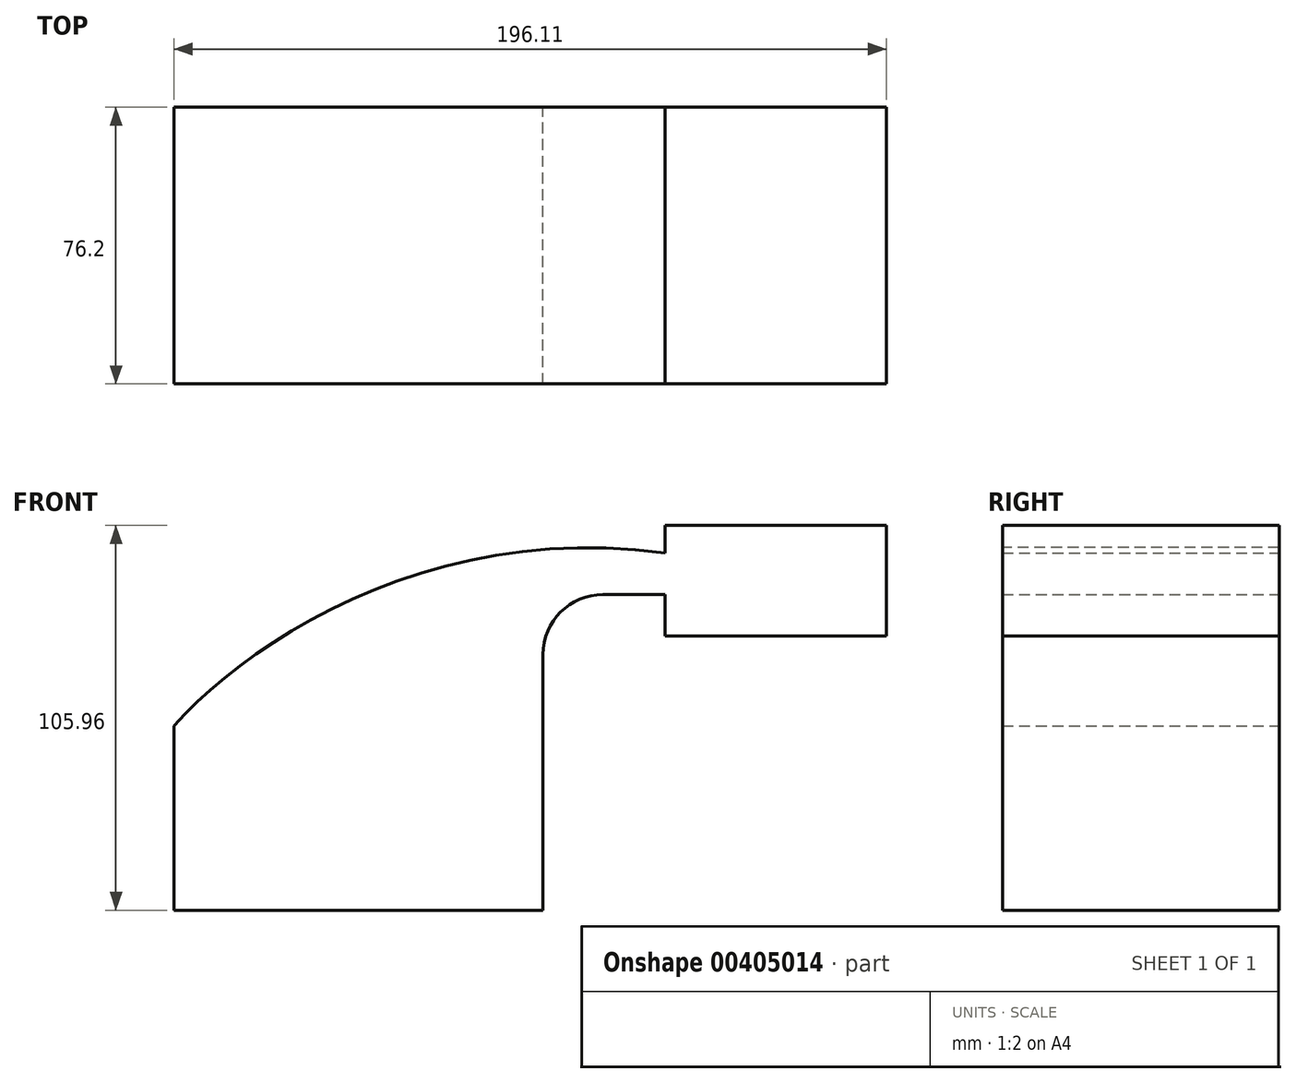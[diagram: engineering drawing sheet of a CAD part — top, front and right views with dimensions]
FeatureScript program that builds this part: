
annotation { "Feature Type Name" : "Feature", "Feature Type Description" : "" }
export const myFeature = defineFeature(function(context is Context, id is Id, definition is map)
    precondition{}
    {
        {
            var Q0;
            Q0=qCreatedBy(makeId("Front.planeOp"),FACE);
            var sketch = newSketch(context, id + "F0", { "sketchPlane" : qUnion([Q0])});
            skLineSegment(sketch, "E0.bottom", {"start": v(50.8, 25.4) * mm, "end": v(-50.8, 25.4) * mm});
            skLineSegment(sketch, "E0.top", {"start": v(50.8, -25.4) * mm, "end": v(-50.8, -25.4) * mm});
            skLineSegment(sketch, "E0.left", {"start": v(50.8, 25.4) * mm, "end": v(50.8, -25.4) * mm});
            skLineSegment(sketch, "E0.right", {"start": v(-50.8, 25.4) * mm, "end": v(-50.8, -25.4) * mm});
            skPoint(sketch, "E0.middle", {"position": v(0, 0) * mm});
            skLineSegment(sketch, "E1.bottom", {"start": v(84.35, 50.08) * mm, "end": v(145.3, 50.08) * mm});
            skLineSegment(sketch, "E1.top", {"start": v(84.35, 80.56) * mm, "end": v(145.3, 80.56) * mm});
            skLineSegment(sketch, "E1.left", {"start": v(84.35, 50.08) * mm, "end": v(84.35, 80.56) * mm});
            skLineSegment(sketch, "E1.right", {"start": v(145.3, 50.08) * mm, "end": v(145.3, 80.56) * mm});
            skPoint(sketch, "E1.middle", {"position": v(114.83, 65.32) * mm});
            skLineSegment(sketch, "E2", {"start": v(50.8, 25.4) * mm, "end": v(50.8, 45.05) * mm});
            skArc(sketch, "E3", {"start": v(50.8, 45.05) * mm, "mid": v(55.64, 56.72) * mm, "end": v(67.31, 61.56) * mm});
            skLineSegment(sketch, "E4", {"start": v(67.31, 61.56) * mm, "end": v(102.87, 61.56) * mm});
            skLineSegment(sketch, "E5.0", {"start": v(67.31, 72.99) * mm, "end": v(102.87, 72.99) * mm});
            skArc(sketch, "E5.1", {"start": v(39.37, 45.05) * mm, "mid": v(47.55, 64.8) * mm, "end": v(67.31, 72.99) * mm});
            skLineSegment(sketch, "E5.2", {"start": v(39.37, 25.4) * mm, "end": v(39.37, 45.05) * mm});
            skLineSegment(sketch, "E6", {"start": v(102.87, 50.08) * mm, "end": v(102.87, 80.56) * mm});
            skFitSpline(sketch, "E7", {"points": [v(-50.8, 25.4) * mm, v(84.35, 72.99) * mm], "startDerivative": vector(65.43, 73.24) * mm, "endDerivative": vector(189.81, -25.95) * mm});
            skSolve(sketch);
        }
        {
            var Q0;
            Q0 = qSketchRegion(id + "F0", true);
            extrude(context, id + "F1", {"entities" : qUnion([Q0]), "endBound" : BoundingType.SYMMETRIC, "depth" : 76.2 * mm});
        }
    });
